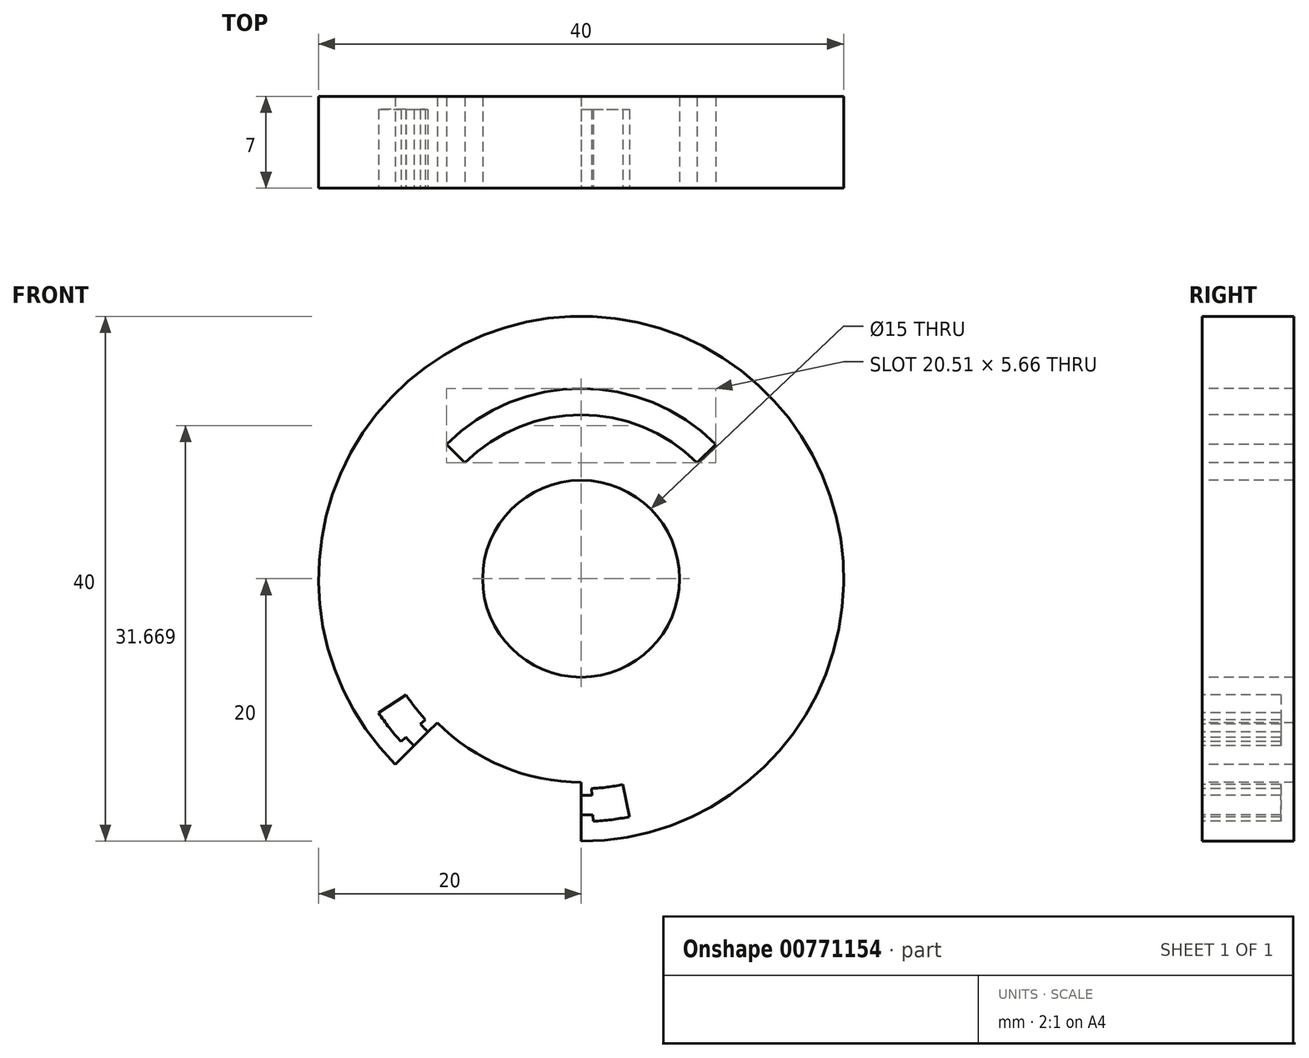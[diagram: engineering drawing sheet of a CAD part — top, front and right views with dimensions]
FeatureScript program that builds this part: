
annotation { "Feature Type Name" : "Feature", "Feature Type Description" : "" }
export const myFeature = defineFeature(function(context is Context, id is Id, definition is map)
    precondition{}
    {
        {
            var Q0;
            Q0=qCreatedBy(makeId("Front.planeOp"),FACE);
            var sketch = newSketch(context, id + "F0", { "sketchPlane" : qUnion([Q0])});
            skCircle(sketch, "E0", {"center": v(0, 0) * mm, "radius": 20 * mm});
            skCircle(sketch, "E1", {"center": v(0, 0) * mm, "radius": 12.5 * mm});
            skCircle(sketch, "E2", {"center": v(0, 0) * mm, "radius": 7.5 * mm});
            skCircle(sketch, "E3", {"center": v(0, 0) * mm, "radius": 14.5 * mm});
            skLineSegment(sketch, "E4", {"start": v(0, 0) * mm, "end": v(14.14, 14.14) * mm});
            skLineSegment(sketch, "E5", {"start": v(0, 0) * mm, "end": v(-14.14, 14.14) * mm});
            skCircle(sketch, "E6", {"center": v(0, 0) * mm, "radius": 15.5 * mm});
            skLineSegment(sketch, "E7", {"start": v(0, 0) * mm, "end": v(-14.14, -14.14) * mm});
            skLineSegment(sketch, "E8", {"start": v(0, 0) * mm, "end": v(0, -20) * mm});
            skSolve(sketch);
        }
        {
            var Q0;
            {var subQ0=sQuery(id+"F0.wireOp",EDGE,"E5");var subQ1=sQuery(id+"F0.wireOp",EDGE,"E0");var subQ2=makeQuery(id+"F0.imprint","INTERSECT",VERTEX,{"derivedFrom":[subQ1,subQ0]});Q0=makeQuery(id+"F0.imprint","IMPRINT",FACE,{"disambiguationData":[TD([[makeQuery(id+"F0.imprint","IMPRINT",EDGE,{"disambiguationData":[TD([[subQ2,-1.0]])],"derivedFrom":subQ1}),1.0]])]});}
            var Q1;
            {var subQ0=sQuery(id+"F0.wireOp",EDGE,"E7");var subQ1=sQuery(id+"F0.wireOp",EDGE,"E3");var subQ2=makeQuery(id+"F0.imprint","INTERSECT",VERTEX,{"derivedFrom":[subQ1,subQ0]});Q1=makeQuery(id+"F0.imprint","IMPRINT",FACE,{"disambiguationData":[TD([[makeQuery(id+"F0.imprint","IMPRINT",EDGE,{"disambiguationData":[TD([[subQ2,-1.0]])],"derivedFrom":subQ1}),-1.0]])]});}
            var Q2;
            {var subQ0=sQuery(id+"F0.wireOp",EDGE,"E4");var subQ1=sQuery(id+"F0.wireOp",EDGE,"E0");var subQ2=makeQuery(id+"F0.imprint","INTERSECT",VERTEX,{"derivedFrom":[subQ1,subQ0]});Q2=makeQuery(id+"F0.imprint","IMPRINT",FACE,{"disambiguationData":[TD([[makeQuery(id+"F0.imprint","IMPRINT",EDGE,{"disambiguationData":[TD([[subQ2,-1.0]])],"derivedFrom":subQ1}),1.0]])]});}
            var Q3;
            {var subQ0=sQuery(id+"F0.wireOp",EDGE,"E4");var subQ1=sQuery(id+"F0.wireOp",EDGE,"E0");var subQ2=makeQuery(id+"F0.imprint","INTERSECT",VERTEX,{"derivedFrom":[subQ1,subQ0]});Q3=makeQuery(id+"F0.imprint","IMPRINT",FACE,{"disambiguationData":[TD([[makeQuery(id+"F0.imprint","IMPRINT",EDGE,{"disambiguationData":[TD([[subQ2,1.0]])],"derivedFrom":subQ1}),1.0]])]});}
            var Q4;
            {var subQ0=sQuery(id+"F0.wireOp",EDGE,"E7");var subQ1=sQuery(id+"F0.wireOp",EDGE,"E1");var subQ2=makeQuery(id+"F0.imprint","INTERSECT",VERTEX,{"derivedFrom":[subQ1,subQ0]});Q4=makeQuery(id+"F0.imprint","IMPRINT",FACE,{"disambiguationData":[TD([[makeQuery(id+"F0.imprint","IMPRINT",EDGE,{"disambiguationData":[TD([[subQ2,-1.0]])],"derivedFrom":subQ1}),-1.0]])]});}
            var Q5;
            {var subQ0=sQuery(id+"F0.wireOp",EDGE,"E7");var subQ1=sQuery(id+"F0.wireOp",EDGE,"E1");var subQ2=makeQuery(id+"F0.imprint","INTERSECT",VERTEX,{"derivedFrom":[subQ1,subQ0]});Q5=makeQuery(id+"F0.imprint","IMPRINT",FACE,{"disambiguationData":[TD([[makeQuery(id+"F0.imprint","IMPRINT",EDGE,{"disambiguationData":[TD([[subQ2,-1.0]])],"derivedFrom":subQ1}),1.0]])]});}
            var Q6;
            {var subQ0=sQuery(id+"F0.wireOp",EDGE,"E5");var subQ1=sQuery(id+"F0.wireOp",EDGE,"E3");var subQ2=makeQuery(id+"F0.imprint","INTERSECT",VERTEX,{"derivedFrom":[subQ1,subQ0]});Q6=makeQuery(id+"F0.imprint","IMPRINT",FACE,{"disambiguationData":[TD([[makeQuery(id+"F0.imprint","IMPRINT",EDGE,{"disambiguationData":[TD([[subQ2,1.0]])],"derivedFrom":subQ1}),-1.0]])]});}
            var Q7;
            {var subQ0=sQuery(id+"F0.wireOp",EDGE,"E5");var subQ1=sQuery(id+"F0.wireOp",EDGE,"E1");var subQ2=makeQuery(id+"F0.imprint","INTERSECT",VERTEX,{"derivedFrom":[subQ1,subQ0]});Q7=makeQuery(id+"F0.imprint","IMPRINT",FACE,{"disambiguationData":[TD([[makeQuery(id+"F0.imprint","IMPRINT",EDGE,{"disambiguationData":[TD([[subQ2,1.0]])],"derivedFrom":subQ1}),1.0]])]});}
            var Q8;
            {var subQ0=sQuery(id+"F0.wireOp",EDGE,"E4");var subQ1=sQuery(id+"F0.wireOp",EDGE,"E1");var subQ2=makeQuery(id+"F0.imprint","INTERSECT",VERTEX,{"derivedFrom":[subQ1,subQ0]});Q8=makeQuery(id+"F0.imprint","IMPRINT",FACE,{"disambiguationData":[TD([[makeQuery(id+"F0.imprint","IMPRINT",EDGE,{"disambiguationData":[TD([[subQ2,1.0]])],"derivedFrom":subQ1}),1.0]])]});}
            var Q9;
            {var subQ0=sQuery(id+"F0.wireOp",EDGE,"E4");var subQ1=sQuery(id+"F0.wireOp",EDGE,"E1");var subQ2=makeQuery(id+"F0.imprint","INTERSECT",VERTEX,{"derivedFrom":[subQ1,subQ0]});Q9=makeQuery(id+"F0.imprint","IMPRINT",FACE,{"disambiguationData":[TD([[makeQuery(id+"F0.imprint","IMPRINT",EDGE,{"disambiguationData":[TD([[subQ2,1.0]])],"derivedFrom":subQ1}),-1.0]])]});}
            var Q10;
            {var subQ0=sQuery(id+"F0.wireOp",EDGE,"E4");var subQ1=sQuery(id+"F0.wireOp",EDGE,"E3");var subQ2=makeQuery(id+"F0.imprint","INTERSECT",VERTEX,{"derivedFrom":[subQ1,subQ0]});Q10=makeQuery(id+"F0.imprint","IMPRINT",FACE,{"disambiguationData":[TD([[makeQuery(id+"F0.imprint","IMPRINT",EDGE,{"disambiguationData":[TD([[subQ2,1.0]])],"derivedFrom":subQ1}),-1.0]])]});}
            var Q11;
            {var subQ0=sQuery(id+"F0.wireOp",EDGE,"E5");var subQ1=sQuery(id+"F0.wireOp",EDGE,"E1");var subQ2=makeQuery(id+"F0.imprint","INTERSECT",VERTEX,{"derivedFrom":[subQ1,subQ0]});Q11=makeQuery(id+"F0.imprint","IMPRINT",FACE,{"disambiguationData":[TD([[makeQuery(id+"F0.imprint","IMPRINT",EDGE,{"disambiguationData":[TD([[subQ2,-1.0]])],"derivedFrom":subQ1}),1.0]])]});}
            var Q12;
            {var subQ0=sQuery(id+"F0.wireOp",EDGE,"E5");var subQ1=sQuery(id+"F0.wireOp",EDGE,"E1");var subQ2=makeQuery(id+"F0.imprint","INTERSECT",VERTEX,{"derivedFrom":[subQ1,subQ0]});Q12=makeQuery(id+"F0.imprint","IMPRINT",FACE,{"disambiguationData":[TD([[makeQuery(id+"F0.imprint","IMPRINT",EDGE,{"disambiguationData":[TD([[subQ2,-1.0]])],"derivedFrom":subQ1}),-1.0]])]});}
            var Q13;
            {var subQ0=sQuery(id+"F0.wireOp",EDGE,"E5");var subQ1=sQuery(id+"F0.wireOp",EDGE,"E3");var subQ2=makeQuery(id+"F0.imprint","INTERSECT",VERTEX,{"derivedFrom":[subQ1,subQ0]});Q13=makeQuery(id+"F0.imprint","IMPRINT",FACE,{"disambiguationData":[TD([[makeQuery(id+"F0.imprint","IMPRINT",EDGE,{"disambiguationData":[TD([[subQ2,-1.0]])],"derivedFrom":subQ1}),-1.0]])]});}
            extrude(context, id + "F1", {"entities" : qUnion([Q0, Q1, Q2, Q3, Q4, Q5, Q6, Q7, Q8, Q9, Q10, Q11, Q12, Q13]), "oppositeDirection" : true, "depth" : 7 * mm, "offsetDistance" : 25 * mm});
        }
        {
            var Q0;
            {var subQ0=sQuery(id+"F0.wireOp",EDGE,"E5");var subQ1=sQuery(id+"F0.wireOp",EDGE,"E0");var subQ2=makeQuery(id+"F0.imprint","INTERSECT",VERTEX,{"derivedFrom":[subQ1,subQ0]});Q0=makeQuery(id+"F0.imprint","IMPRINT",FACE,{"disambiguationData":[TD([[makeQuery(id+"F0.imprint","IMPRINT",EDGE,{"disambiguationData":[TD([[subQ2,-1.0]])],"derivedFrom":subQ1}),1.0]])]});}
            var sketch = newSketch(context, id + "F2", { "sketchPlane" : qUnion([Q0])});
            skLineSegment(sketch, "E9.0", {"start": v(0, 0) * mm, "end": v(-14.14, -14.14) * mm});
            skCircle(sketch, "E10.0", {"center": v(0, 0) * mm, "radius": 20 * mm});
            skCircle(sketch, "E11.0", {"center": v(0, 0) * mm, "radius": 15.5 * mm});
            skLineSegment(sketch, "E12", {"start": v(0, 0) * mm, "end": v(-14.83, -13.42) * mm});
            skLineSegment(sketch, "E13", {"start": v(0, 0) * mm, "end": v(-16.67, -11.05) * mm});
            skCircle(sketch, "E14", {"center": v(0, 0) * mm, "radius": 16 * mm});
            skCircle(sketch, "E15", {"center": v(0, 0) * mm, "radius": 16.5 * mm});
            skCircle(sketch, "E16", {"center": v(0, 0) * mm, "radius": 18 * mm});
            skCircle(sketch, "E17", {"center": v(0, 0) * mm, "radius": 18.5 * mm});
            skLineSegment(sketch, "E18", {"start": v(0, 0) * mm, "end": v(1, -19.97) * mm});
            skLineSegment(sketch, "E19", {"start": v(0, 0) * mm, "end": v(3.98, -19.6) * mm});
            skSolve(sketch);
        }
        {
            var Q0;
            {var subQ0=sQuery(id+"F2.wireOp",EDGE,"E15");var subQ1=sQuery(id+"F2.wireOp",EDGE,"E9.0");var subQ2=makeQuery(id+"F2.imprint","INTERSECT",VERTEX,{"derivedFrom":[subQ1,subQ0]});Q0=makeQuery(id+"F2.imprint","IMPRINT",FACE,{"disambiguationData":[TD([[makeQuery(id+"F2.imprint","IMPRINT",EDGE,{"disambiguationData":[TD([[subQ2,-1.0]])],"derivedFrom":subQ1}),-1.0]])]});}
            var Q1;
            {var subQ0=sQuery(id+"F2.wireOp",EDGE,"E16");var subQ1=sQuery(id+"F2.wireOp",EDGE,"E12");var subQ2=makeQuery(id+"F2.imprint","INTERSECT",VERTEX,{"derivedFrom":[subQ1,subQ0]});Q1=makeQuery(id+"F2.imprint","IMPRINT",FACE,{"disambiguationData":[TD([[makeQuery(id+"F2.imprint","IMPRINT",EDGE,{"disambiguationData":[TD([[subQ2,-1.0]])],"derivedFrom":subQ1}),-1.0]])]});}
            var Q2;
            {var subQ0=sQuery(id+"F2.wireOp",EDGE,"E15");var subQ1=sQuery(id+"F2.wireOp",EDGE,"E12");var subQ2=makeQuery(id+"F2.imprint","INTERSECT",VERTEX,{"derivedFrom":[subQ1,subQ0]});Q2=makeQuery(id+"F2.imprint","IMPRINT",FACE,{"disambiguationData":[TD([[makeQuery(id+"F2.imprint","IMPRINT",EDGE,{"disambiguationData":[TD([[subQ2,-1.0]])],"derivedFrom":subQ1}),-1.0]])]});}
            var Q3;
            {var subQ0=sQuery(id+"F2.wireOp",EDGE,"E14");var subQ1=sQuery(id+"F2.wireOp",EDGE,"E12");var subQ2=makeQuery(id+"F2.imprint","INTERSECT",VERTEX,{"derivedFrom":[subQ1,subQ0]});Q3=makeQuery(id+"F2.imprint","IMPRINT",FACE,{"disambiguationData":[TD([[makeQuery(id+"F2.imprint","IMPRINT",EDGE,{"disambiguationData":[TD([[subQ2,-1.0]])],"derivedFrom":subQ1}),-1.0]])]});}
            var Q4;
            {var subQ0=sQuery(id+"F2.wireOp",EDGE,"E15");var subQ1=sQuery(id+"F2.wireOp",EDGE,"E9.0");var subQ2=makeQuery(id+"F2.imprint","INTERSECT",VERTEX,{"derivedFrom":[subQ1,subQ0]});Q4=makeQuery(id+"F2.imprint","IMPRINT",FACE,{"disambiguationData":[TD([[makeQuery(id+"F2.imprint","IMPRINT",EDGE,{"disambiguationData":[TD([[subQ2,-1.0]])],"derivedFrom":subQ1}),1.0]])]});}
            var Q5;
            {var subQ0=sQuery(id+"F2.wireOp",EDGE,"E18");var subQ1=sQuery(id+"F2.wireOp",EDGE,"E15");var subQ2=makeQuery(id+"F2.imprint","INTERSECT",VERTEX,{"derivedFrom":[subQ1,subQ0]});Q5=makeQuery(id+"F2.imprint","IMPRINT",FACE,{"disambiguationData":[TD([[makeQuery(id+"F2.imprint","IMPRINT",EDGE,{"disambiguationData":[TD([[subQ2,-1.0]])],"derivedFrom":subQ1}),-1.0]])]});}
            var Q6;
            {var subQ0=sQuery(id+"F2.wireOp",EDGE,"E18");var subQ1=sQuery(id+"F2.wireOp",EDGE,"E14");var subQ2=makeQuery(id+"F2.imprint","INTERSECT",VERTEX,{"derivedFrom":[subQ1,subQ0]});Q6=makeQuery(id+"F2.imprint","IMPRINT",FACE,{"disambiguationData":[TD([[makeQuery(id+"F2.imprint","IMPRINT",EDGE,{"disambiguationData":[TD([[subQ2,-1.0]])],"derivedFrom":subQ1}),-1.0]])]});}
            var Q7;
            {var subQ0=sQuery(id+"F2.wireOp",EDGE,"E18");var subQ1=sQuery(id+"F2.wireOp",EDGE,"E16");var subQ2=makeQuery(id+"F2.imprint","INTERSECT",VERTEX,{"derivedFrom":[subQ1,subQ0]});Q7=makeQuery(id+"F2.imprint","IMPRINT",FACE,{"disambiguationData":[TD([[makeQuery(id+"F2.imprint","IMPRINT",EDGE,{"disambiguationData":[TD([[subQ2,-1.0]])],"derivedFrom":subQ1}),-1.0]])]});}
            extrude(context, id + "F3", {"entities" : qUnion([Q0, Q1, Q2, Q3, Q4, Q5, Q6, Q7]), "operationType" : NewBodyOperationType.REMOVE, "oppositeDirection" : true, "depth" : 6 * mm, "offsetDistance" : 25 * mm});
        }
    });
